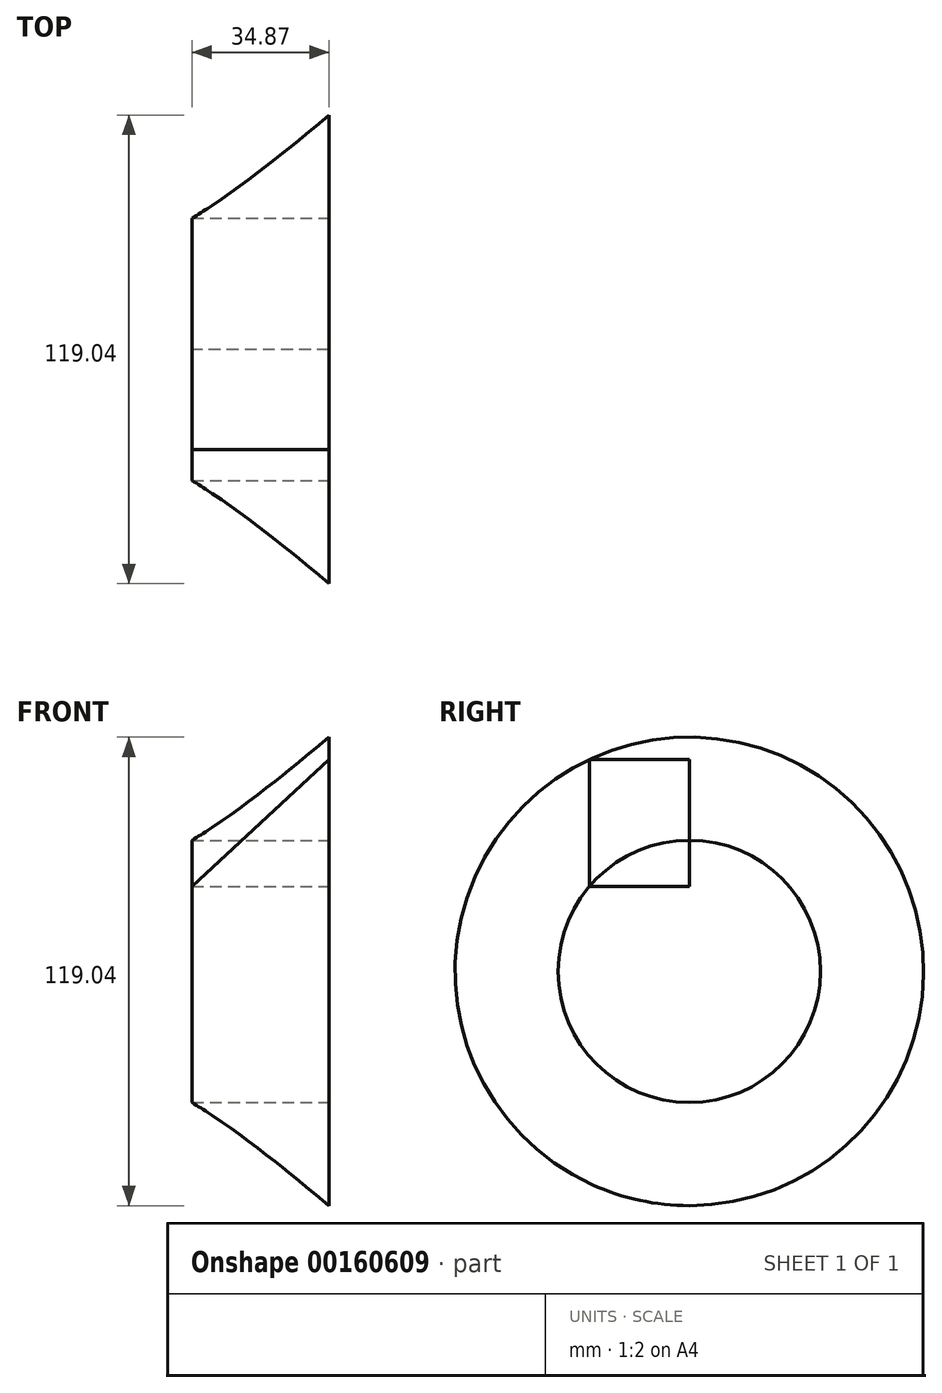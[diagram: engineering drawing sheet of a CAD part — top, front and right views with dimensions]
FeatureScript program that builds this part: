
annotation { "Feature Type Name" : "Feature", "Feature Type Description" : "" }
export const myFeature = defineFeature(function(context is Context, id is Id, definition is map)
    precondition{}
    {
        {
            var Q0;
            Q0=qCreatedBy(makeId("Front.planeOp"),FACE);
            var sketch = newSketch(context, id + "F0", { "sketchPlane" : qUnion([Q0])});
            skLineSegment(sketch, "E0", {"start": v(-29.6, 41.47) * mm, "end": v(-51.13, 21.55) * mm});
            skLineSegment(sketch, "E1", {"start": v(-51.13, 21.55) * mm, "end": v(-16.26, 21.55) * mm});
            skLineSegment(sketch, "E2", {"start": v(-16.26, 21.55) * mm, "end": v(-16.26, 53.82) * mm});
            skLineSegment(sketch, "E3", {"start": v(-16.26, 53.82) * mm, "end": v(-31.53, 39.69) * mm});
            skLineSegment(sketch, "E4", {"start": v(0, 0) * mm, "end": v(0, 57.8) * mm});
            skSolve(sketch);
        }
        {
            var Q0;
            Q0 = qSketchRegion(id + "F0", true);
            extrude(context, id + "F1", {"entities" : qUnion([Q0]), "depth" : 25.4 * mm});
        }
        {
            var Q0;
            Q0=qCreatedBy(makeId("Top.planeOp"),FACE);
            var sketch = newSketch(context, id + "F2", { "sketchPlane" : qUnion([Q0])});
            skLineSegment(sketch, "E5", {"start": v(0, -22.83) * mm, "end": v(0, 20.62) * mm});
            skLineSegment(sketch, "E6", {"start": v(0, 0) * mm, "end": v(21.77, 0) * mm});
            skLineSegment(sketch, "E7", {"start": v(21.77, 0) * mm, "end": v(-17.55, 0) * mm});
            skSolve(sketch);
        }
        {
            var Q0;
            Q0=makeQuery(id+"F1.opExtrude","CAP_FACE",FACE,{"disambiguationData":[OSD([sQuery(id+"F0.wireOp",EDGE,"E0"),sQuery(id+"F0.wireOp",EDGE,"E1"),sQuery(id+"F0.wireOp",EDGE,"E2"),sQuery(id+"F0.wireOp",EDGE,"E3")])],"isStart":false});
            var Q1;
            Q1=sQuery(id+"F2.wireOp",EDGE,"E7");
            revolve(context, id + "F3", {"entities" : qUnion([Q0]), "axis" : qUnion([Q1]), "revolveType" : RevolveType.FULL});
        }
    });
